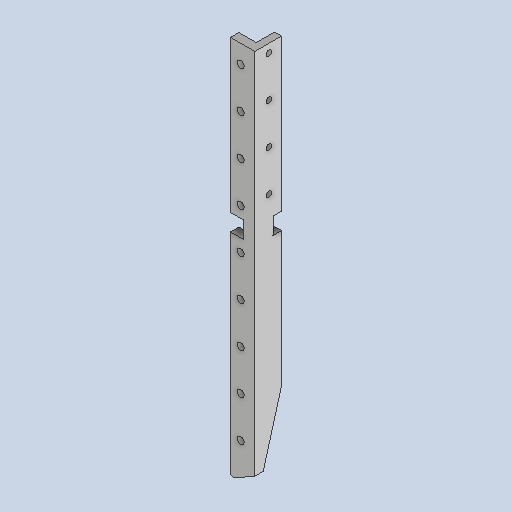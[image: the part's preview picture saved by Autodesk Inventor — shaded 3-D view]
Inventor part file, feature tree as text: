
AUTODESK INVENTOR PART (.ipt)
format: ipt  version: 2025.1 (Build 291241000, 241)  size: 347,136 bytes
history: native  units: mm
features: sketch x6, extrude x4, hole x2, fillet x1, projected_geometry x1
ambient origin geometry x8: Origin, YZ Plane, XZ Plane, XY Plane, X Axis, Y Axis, Z Axis, Center Point
bodies: Solid1 (feature_tree)
feature tree (14):
  extrude  "Extrusion1"  TaperAngle=60.0deg  [1 undecoded]
  hole  "Hole1"  [1 undecoded]
  extrude  "Extrusion2"  Depth=262.0mm
  extrude  "Extrusion3"  Depth=10.0mm
  hole  "Hole2"  [1 undecoded]
  extrude  "Extrusion4"  Depth=2.0mm
  fillet  "Fillet1"  Radius=29.0mm
  sketch  "Sketch1"  dims[d0=272.0mm d1=60.0deg]
  sketch  "Sketch2"  dims[d2=12.0mm d3=9.0mm]
  sketch  "Sketch3"  dims[d4=108.0mm d6=262.0mm]
  sketch  "Sketch4"  dims[d7=6.0mm d8=0.0mm d9=10.0mm]
  sketch  "Sketch5"  dims[d10=17.0mm d11=13.0mm]
  sketch  "Sketch6"  dims[d12=29.0mm d13=29.0mm d14=29.0mm d15=29.0mm d16=29.0mm d17=29.0mm d18=29.0mm d19=29.0mm d20=5.0mm d21=6.0mm d22=4.0mm d23=2.0mm d24=90.0deg d25=8.0mm d26=0.0mm d27=5.0mm d28=13.0mm d29=0.0mm d30=12.0mm d31=6.0mm d32=108.0mm d33=5.0mm d34=0.0mm d35=6.0mm d36=15.0mm d37=29.0mm d38=29.0mm d39=29.0mm d40=10.0mm d41=4.0mm d42=6.0mm d43=5.0mm d44=2.0mm d45=90.0deg d46=8.0mm d47=0.0mm d48=96.0mm d49=20.0mm d50=0.0mm d51=2.0mm]
  projected_geometry  "Projected Loop1"
note: 3 required parameter values undecoded (feature->parameter linkage not recoverable at this tier; creation-order binding heuristic only, values carry confidence <= 0.55)
